FCSTD DOCUMENT  (FreeCAD 0.21R33771 (Git))
Label: key-v4_reall
License: All rights reserved
LicenseURL: https://en.wikipedia.org/wiki/All_rights_reserved
objects: Part::Part2DObjectPython×3, Sketcher::SketchObject×3, Spreadsheet::Sheet×1
note: 6 computed .brp shape members not serialized (recipe doc carries the construction recipe); baked Part::Feature solids carry a one-line shape summary decoded from their .brp

FEATURE [Spreadsheet::Sheet] Spreadsheet  label="constants"
  cells = A1(slot_height)=0.6; B1='slot height; A2(base_normal)=1.5; B2='base normal; A3(base_thin)=0.3; B3='base thin ; A4(fillet_small)=0.15; B4='fillet rounding
FEATURE [Part::Part2DObjectPython] Wire  # Draft 2D object (typed FeaturePython)
  Area = 0
  ChamferSize = 0
  Closed = false
  End = (95,2.6,0)
  FilletRadius = 0
  Length = 95.9778
  MakeFace = true
  Points = (6) [(0,0,0),(19,0,0),(38,4.8,0),(57,7,0),(76,4.8,0),(95,2.6,0)]
  Start = (0,0,0)
  Subdivisions = 0
FEATURE [Part::Part2DObjectPython] Wire001  label="main matrix wire"  # Draft 2D object (typed FeaturePython)
  Area = 0
  ChamferSize = 0
  Closed = false
  End = (95,2.6,0)
  FilletRadius = 0
  Length = 323.978
  MakeFace = false
  Points = (18) [(0,0,0),(0,-19,0),(0,-38,0),(19,-38,0),(19,-19,0),(19,0,0),(38,4.8,0),(38,-14.2,0),(38,-33.2,0),(57,-31,0),(57,-12,0),(57,7,0),(76,4.8,0),+5 more]
  Start = (0,0,0)
  Subdivisions = 0
FEATURE [Part::Part2DObjectPython] Wire002  label="horizonal matrix"  # Draft 2D object (typed FeaturePython)
  Area = 0
  ChamferSize = 0
  Closed = false
  End = (95,2.6,0)
  FilletRadius = 0
  Length = 368.271
  MakeFace = true
  Points = (20) [(0,0,0),(0,-19,0),(0,-38,0),(19,-38,0),(19,-19,0),(19,0,0),(38,4.8,0),(38,-14.2,0),(38,-33.2,0),(47,-52.4,0),(66,-52.4,0),(57,-31,0),(57,-12,0),+7 more]
  Start = (0,0,0)
  Subdivisions = 0
FEATURE [Sketcher::SketchObject] Sketch001  label="smd cutout prototype"
  FullyConstrained = true
  sketch-geometry (67):
    g0: LineSegment StartX=-9.5 StartY=-9.5 StartZ=0 EndX=9.5 EndY=-9.5 EndZ=0
    g1: LineSegment StartX=9.5 StartY=-9.5 StartZ=0 EndX=9.5 EndY=9.5 EndZ=0
    g2: LineSegment StartX=9.5 StartY=9.5 StartZ=0 EndX=-9.5 EndY=9.5 EndZ=0
    g3: LineSegment StartX=-9.5 StartY=9.5 StartZ=0 EndX=-9.5 EndY=-9.5 EndZ=0
    g4: Circle CenterX=-3.81 CenterY=2.54 CenterZ=0 NormalX=0 NormalY=0 NormalZ=1 AngleXU=0 Radius=1.5
    g5: Circle CenterX=2.54 CenterY=5.08 CenterZ=0 NormalX=0 NormalY=0 NormalZ=1 AngleXU=0 Radius=1.5
    g6: Circle CenterX=0 CenterY=0 CenterZ=0 NormalX=0 NormalY=0 NormalZ=1 AngleXU=0 Radius=2
    g7: Circle CenterX=5 CenterY=0 CenterZ=0 NormalX=0 NormalY=0 NormalZ=1 AngleXU=0 Radius=1
    g8: Circle CenterX=-5 CenterY=0 CenterZ=0 NormalX=0 NormalY=0 NormalZ=1 AngleXU=0 Radius=1
    g9: GeomPoint X=-8.5 Y=1 Z=0
    g10: GeomPoint X=-8.5 Y=4 Z=0
    g11: GeomPoint X=-6 Y=4 Z=0
    g12: GeomPoint X=-2.5 Y=1 Z=0
    g13: GeomPoint X=-0.4 Y=2.9 Z=0
    g14: GeomPoint X=4.5 Y=2.9 Z=0
    g15: GeomPoint X=4.5 Y=3.6 Z=0
    g16: GeomPoint X=7.1 Y=6.7 Z=0
    g17: GeomPoint X=-4 Y=6.7 Z=0
    g18: LineSegment StartX=-8.5 StartY=1 StartZ=0 EndX=-2.5 EndY=1 EndZ=0
    g19: LineSegment StartX=-8.5 StartY=1 StartZ=0 EndX=-8.5 EndY=4 EndZ=0
    g20: LineSegment StartX=-8.5 StartY=4 StartZ=0 EndX=-6 EndY=4 EndZ=0
    g21: LineSegment StartX=-6 StartY=4 StartZ=0 EndX=-6 EndY=4.7 EndZ=0
    g22: LineSegment StartX=-4 StartY=6.7 StartZ=0 EndX=7.1 EndY=6.7 EndZ=0
    g23: LineSegment StartX=7.1 StartY=6.7 StartZ=0 EndX=7.1 EndY=3.6 EndZ=0
    g24: LineSegment StartX=7.1 StartY=3.6 StartZ=0 EndX=4.5 EndY=3.6 EndZ=0
    g25: LineSegment StartX=4.5 StartY=2.9 StartZ=0 EndX=4.5 EndY=3.6 EndZ=0
    g26: LineSegment StartX=4.5 StartY=2.9 StartZ=0 EndX=-0.4 EndY=2.9 EndZ=0
    g27: ArcOfCircle CenterX=-0.4 CenterY=0.789474 CenterZ=0 NormalX=0 NormalY=0 NormalZ=1 AngleXU=0 Radius=2.11053 StartAngle=1.5708 EndAngle=3.04168
    g28: LineSegment StartX=6.85 StartY=2.35 StartZ=0 EndX=6.85 EndY=-2.35 EndZ=0
    g29: LineSegment StartX=6.85 StartY=-2.35 StartZ=0 EndX=9.15 EndY=-2.35 EndZ=0
    g30: LineSegment StartX=9.15 StartY=-2.35 StartZ=0 EndX=9.15 EndY=2.35 EndZ=0
    g31: ArcOfCircle CenterX=-4 CenterY=4.7 CenterZ=0 NormalX=0 NormalY=0 NormalZ=1 AngleXU=0 Radius=2 StartAngle=1.5708 EndAngle=3.14159
    g32: LineSegment StartX=6.85 StartY=2.35 StartZ=0 EndX=9.15 EndY=2.35 EndZ=0
    g33: LineSegment StartX=-8.8 StartY=0.8 StartZ=0 EndX=-8.8 EndY=4.2 EndZ=0
    g34: LineSegment StartX=-8.3 StartY=4.7 StartZ=0 EndX=-7.1607 EndY=4.7 EndZ=0
    g35: LineSegment StartX=-4 StartY=7.4 StartZ=0 EndX=7.3 EndY=7.4 EndZ=0
    g36: LineSegment StartX=7.8 StartY=6.9 StartZ=0 EndX=7.8 EndY=3.55 EndZ=0
    g37: LineSegment StartX=9.5 StartY=2.55 StartZ=0 EndX=9.5 EndY=-2.55 EndZ=0
    g38: LineSegment StartX=9 StartY=-3.05 StartZ=0 EndX=6.65 EndY=-3.05 EndZ=0
    g39: LineSegment StartX=-8.3 StartY=0.3 StartZ=0 EndX=-7.19089 EndY=0.3 EndZ=0
    g40: ArcOfCircle CenterX=-5 CenterY=0 CenterZ=0 NormalX=0 NormalY=0 NormalZ=1 AngleXU=0 Radius=1.7 StartAngle=3.23263 EndAngle=4.71239
    g41: ArcOfCircle CenterX=0 CenterY=0 CenterZ=0 NormalX=0 NormalY=0 NormalZ=1 AngleXU=0 Radius=2.7 StartAngle=3.89963 EndAngle=5.52514
    g42: LineSegment StartX=-5 StartY=-1.7 StartZ=0 EndX=-2.32379 EndY=-1.7 EndZ=0
    g43: LineSegment StartX=6.15 StartY=-2.55 StartZ=0 EndX=6.15 EndY=-2.2 EndZ=0
    g44: LineSegment StartX=2.32379 StartY=-1.7 StartZ=0 EndX=5.65 EndY=-1.7 EndZ=0
    g45: ArcOfCircle CenterX=-4 CenterY=4.7 CenterZ=0 NormalX=0 NormalY=0 NormalZ=1 AngleXU=0 Radius=2.7 StartAngle=1.5708 EndAngle=2.9847
    g46: ArcOfCircle CenterX=-2.32379 CenterY=-2.2 CenterZ=0 NormalX=0 NormalY=0 NormalZ=1 AngleXU=0 Radius=0.5 StartAngle=0.758041 EndAngle=1.5708
    g47: ArcOfCircle CenterX=2.32379 CenterY=-2.2 CenterZ=0 NormalX=0 NormalY=0 NormalZ=1 AngleXU=0 Radius=0.5 StartAngle=1.5708 EndAngle=2.38355
    g48: ArcOfCircle CenterX=5.65 CenterY=-2.2 CenterZ=0 NormalX=0 NormalY=0 NormalZ=1 AngleXU=0 Radius=0.5 StartAngle=0 EndAngle=1.5708
    g49: GeomPoint X=6.15 Y=-1.7 Z=0
    g50: ArcOfCircle CenterX=6.65 CenterY=-2.55 CenterZ=0 NormalX=0 NormalY=0 NormalZ=1 AngleXU=0 Radius=0.5 StartAngle=3.14159 EndAngle=4.71239
    g51: GeomPoint X=6.15 Y=-3.05 Z=0
    g52: ArcOfCircle CenterX=9 CenterY=-2.55 CenterZ=0 NormalX=0 NormalY=0 NormalZ=1 AngleXU=0 Radius=0.5 StartAngle=4.71239 EndAngle=6.28319
    g53: GeomPoint X=9.5 Y=-3.05 Z=0
    g54: LineSegment StartX=8.3 StartY=3.05 StartZ=0 EndX=9 EndY=3.05 EndZ=0
    g55: ArcOfCircle CenterX=9 CenterY=2.55 CenterZ=0 NormalX=0 NormalY=0 NormalZ=1 AngleXU=0 Radius=0.5 StartAngle=3e-16 EndAngle=1.5708
    g56: GeomPoint X=9.5 Y=3.05 Z=0
    g57: ArcOfCircle CenterX=8.3 CenterY=3.55 CenterZ=0 NormalX=0 NormalY=0 NormalZ=1 AngleXU=0 Radius=0.5 StartAngle=3.14159 EndAngle=4.71239
    g58: GeomPoint X=7.8 Y=3.05 Z=0
    g59: ArcOfCircle CenterX=7.3 CenterY=6.9 CenterZ=0 NormalX=0 NormalY=0 NormalZ=1 AngleXU=0 Radius=0.5 StartAngle=-9e-16 EndAngle=1.5708
    g60: GeomPoint X=7.8 Y=7.4 Z=0
    g61: ArcOfCircle CenterX=-7.1607 CenterY=5.2 CenterZ=0 NormalX=0 NormalY=0 NormalZ=1 AngleXU=0 Radius=0.5 StartAngle=4.71239 EndAngle=6.12629
    g62: ArcOfCircle CenterX=-8.3 CenterY=4.2 CenterZ=0 NormalX=0 NormalY=0 NormalZ=1 AngleXU=0 Radius=0.5 StartAngle=1.5708 EndAngle=3.14159
    g63: GeomPoint X=-8.8 Y=4.7 Z=0
    g64: ArcOfCircle CenterX=-8.3 CenterY=0.8 CenterZ=0 NormalX=0 NormalY=0 NormalZ=1 AngleXU=0 Radius=0.5 StartAngle=3.14159 EndAngle=4.71239
    g65: GeomPoint X=-8.8 Y=0.3 Z=0
    g66: ArcOfCircle CenterX=-7.19089 CenterY=-0.2 CenterZ=0 NormalX=0 NormalY=0 NormalZ=1 AngleXU=0 Radius=0.5 StartAngle=0.0910348 EndAngle=1.5708
  constraints (157):
    c: Coincident(g2,g3)
    c: Horizontal(g0)
    c: Horizontal(g2)
    c: Vertical(g1)
    c: PointOnObject(g7,g-1)
    c: Equal(g4,g5)
    c: Symmetric(g7,g8,g-2)
    c: Equal(g8,g7)
    c: DistanceX(g-1,g5) = 2.54
    c: Distance(g5,g-1) = 5.08
    c: DistanceX(g2,g2) = 19
    c: Equal(g2,g3)
    c: Distance(g4,g-2) = 3.81
    c: Distance(g4,g-1) = 2.54
    c: Distance(g8,g-2) = 5
    c: Distance(g9,g-1) = 1
    c: Coincident(g18,g9)
    c: Coincident(g18,g12)
    c: Horizontal(g18)
    c: Distance(g9,g-2) = 8.5
    c: Coincident(g19,g9)
    c: Coincident(g19,g10)
    c: Vertical(g19)
    c: Distance(g10,g-1) = 4
    c: Coincident(g20,g10)
    c: Coincident(g20,g11)
    c: Horizontal(g20)
    c: Distance(g11,g-2) = 6
    c: Distance(g17,g-2) = 4
    c: DistanceY(g-1,g17) = 6.7
    c: Coincident(g21,g11)
    c: Vertical(g21)
    c: Coincident(g22,g17)
    c: Coincident(g22,g16)
    c: Horizontal(g22)
    c: DistanceX(g-1,g16) = 7.1
    c: Coincident(g23,g16)
    c: Vertical(g23)
    c: Distance(g23,g-1) = 3.6
    c: Coincident(g24,g23)
    c: Coincident(g24,g15)
    c: Coincident(g25,g14)
    c: Coincident(g25,g15)
    c: Coincident(g26,g14)
    c: Coincident(g26,g13)
    c: Horizontal(g24)
    c: Horizontal(g26)
    c: Vertical(g25)
    c: Distance(g-2,g25) = 4.5
    c: Distance(g14,g-1) = 2.9
    c: Distance(g13,g-2) = 0.4
    c: Distance(g12,g-2) = 2.5
    c: Coincident(g27,g13)
    c: Coincident(g27,g12)
    c: Diameter(g5) = 3
    c: Diameter(g8) = 2
    c: Diameter(g6) = 4
    c: Vertical(g30)
    c: Horizontal(g29)
    c: Distance(g28,g-2) = 6.85
    c: Distance(g28,g-1) = 2.35
    c: Symmetric(g28,g28,g-1)
    c: Vertical(g3)
    c: Coincident(g31,g17)
    c: Tangent(g31,g21) = 1.5708
    c: Coincident(g32,g28)
    c: Coincident(g32,g30)
    c: Horizontal(g32)
    c: Coincident(g6,g-1)
    c: Symmetric(g0,g1,g6)
    c: Coincident(g3,g0)
    c: Coincident(g2,g1)
    c: Coincident(g1,g0)
    c: DistanceX(g29,g29) = 2.3
    c: Coincident(g29,g30)
    c: Coincident(g29,g28)
    c: Tangent(g27,g26)
    c: Tangent(g31,g22)
    c: Vertical(g33)
    c: Horizontal(g34)
    c: Horizontal(g35)
    c: Vertical(g36)
    c: PointOnObject(g56,g1)
    c: PointOnObject(g53,g1)
    c: Horizontal(g38)
    c: Horizontal(g39)
    c: Distance(g20,g34) = 0.7
    c: Distance(g65,g19) = 0.3
    c: Distance(g18,g39) = 0.7
    c: Coincident(g40,g8)
    c: Coincident(g41,g6)
    c: Horizontal(g42)
    c: Vertical(g43)
    c: Tangent(g44,g42)
    c: Distance(g28,g43) = 0.7
    c: Distance(g53,g29) = 0.7
    c: Tangent(g42,g40) = -1.5708
    c: Distance(g23,g36) = 0.7
    c: Distance(g35,g22) = 0.7
    c: Coincident(g45,g31)
    c: Tangent(g45,g35) = 1.5708
    c: Tangent(g42,g46) = 1.5708
    c: Tangent(g41,g46) = 1.5708
    c: Tangent(g41,g47) = 1.5708
    c: Tangent(g44,g47) = 1.5708
    c: PointOnObject(g49,g44)
    c: PointOnObject(g49,g43)
    c: Tangent(g44,g48) = 1.5708
    c: Tangent(g43,g48) = -1.5708
    c: PointOnObject(g51,g43)
    c: PointOnObject(g51,g38)
    c: Tangent(g43,g50) = 1.5708
    c: Tangent(g38,g50) = 1.5708
    c: PointOnObject(g53,g38)
    c: PointOnObject(g53,g37)
    c: Tangent(g38,g52) = 1.5708
    c: Tangent(g37,g52) = 1.5708
    c: Horizontal(g54)
    c: Distance(g32,g54) = 0.7
    c: PointOnObject(g56,g37)
    c: PointOnObject(g56,g54)
    c: Tangent(g37,g55) = 1.5708
    c: Tangent(g54,g55) = 1.5708
    c: PointOnObject(g58,g54)
    c: PointOnObject(g58,g36)
    c: Tangent(g54,g57) = -1.5708
    c: Tangent(g36,g57) = -1.5708
    c: PointOnObject(g60,g35)
    c: PointOnObject(g60,g36)
    c: Tangent(g35,g59) = 1.5708
    c: Tangent(g36,g59) = 1.5708
    c: Tangent(g34,g61) = -1.5708
    c: Tangent(g45,g61) = 1.5708
    c: PointOnObject(g63,g34)
    c: PointOnObject(g63,g33)
    c: Tangent(g34,g62) = 1.5708
    c: Tangent(g33,g62) = 1.5708
    c: PointOnObject(g65,g39)
    c: PointOnObject(g65,g33)
    c: Tangent(g39,g64) = -1.5708
    c: Tangent(g33,g64) = 1.5708
    c: Tangent(g40,g66) = 1.5708
    c: Tangent(g39,g66) = 1.5708
    c: Radius(g46) = 0.5
    c: Equal(g66,g64)
    c: Equal(g64,g46)
    c: Equal(g46,g47)
    c: Equal(g47,g48)
    c: Equal(g48,g50)
    c: Equal(g50,g57)
    c: Equal(g57,g59)
    c: Equal(g59,g61)
    c: Equal(g61,g62)
    c: Equal(g57,g55)
    c: Equal(g52,g50)
    c: Distance(g40,g8) = 0.7
    c: Distance(g41,g6) = 0.7
FEATURE [Sketcher::SketchObject] Sketch003  label="smd cutout"
  FullyConstrained = false
  sketch-geometry (61):
    g0: GeomPoint X=-8.5 Y=1 Z=0
    g1: GeomPoint X=-8.5 Y=4 Z=0
    g2: GeomPoint X=-6 Y=4 Z=0
    g3: GeomPoint X=-2.5 Y=1 Z=0
    g4: GeomPoint X=-0.4 Y=2.9 Z=0
    g5: GeomPoint X=4.5 Y=2.9 Z=0
    g6: GeomPoint X=4.5 Y=3.6 Z=0
    g7: GeomPoint X=7.1 Y=6.7 Z=0
    g8: GeomPoint X=-4 Y=6.7 Z=0
    g9: LineSegment StartX=-8.8 StartY=0.8 StartZ=0 EndX=-8.8 EndY=4.2 EndZ=0
    g10: LineSegment StartX=-8.3 StartY=4.7 StartZ=0 EndX=-7.1607 EndY=4.7 EndZ=0
    g11: LineSegment StartX=-4 StartY=7.4 StartZ=0 EndX=7.3 EndY=7.4 EndZ=0
    g12: LineSegment StartX=7.8 StartY=6.9 StartZ=0 EndX=7.8 EndY=3.55 EndZ=0
    g13: LineSegment StartX=9.5 StartY=2.55 StartZ=0 EndX=9.5 EndY=-2.55 EndZ=0
    g14: LineSegment StartX=9 StartY=-3.05 StartZ=0 EndX=6.65 EndY=-3.05 EndZ=0
    g15: LineSegment StartX=-8.3 StartY=0.3 StartZ=0 EndX=-7.19089 EndY=0.3 EndZ=0
    g16: ArcOfCircle CenterX=-5 CenterY=0 CenterZ=0 NormalX=0 NormalY=0 NormalZ=1 AngleXU=0 Radius=1.7 StartAngle=3.23263 EndAngle=4.71239
    g17: ArcOfCircle CenterX=0 CenterY=0 CenterZ=0 NormalX=0 NormalY=0 NormalZ=1 AngleXU=0 Radius=2.7 StartAngle=3.89963 EndAngle=5.52514
    g18: LineSegment StartX=-5 StartY=-1.7 StartZ=0 EndX=-2.32379 EndY=-1.7 EndZ=0
    g19: LineSegment StartX=6.15 StartY=-2.55 StartZ=0 EndX=6.15 EndY=-2.2 EndZ=0
    g20: LineSegment StartX=2.32379 StartY=-1.7 StartZ=0 EndX=5.65 EndY=-1.7 EndZ=0
    g21: ArcOfCircle CenterX=-4 CenterY=4.7 CenterZ=0 NormalX=0 NormalY=0 NormalZ=1 AngleXU=0 Radius=2.7 StartAngle=1.5708 EndAngle=2.9847
    g22: ArcOfCircle CenterX=-2.32379 CenterY=-2.2 CenterZ=0 NormalX=0 NormalY=0 NormalZ=1 AngleXU=0 Radius=0.5 StartAngle=0.758041 EndAngle=1.5708
    g23: ArcOfCircle CenterX=2.32379 CenterY=-2.2 CenterZ=0 NormalX=0 NormalY=0 NormalZ=1 AngleXU=0 Radius=0.5 StartAngle=1.5708 EndAngle=2.38355
    g24: ArcOfCircle CenterX=5.65 CenterY=-2.2 CenterZ=0 NormalX=0 NormalY=0 NormalZ=1 AngleXU=0 Radius=0.5 StartAngle=0 EndAngle=1.5708
    g25: GeomPoint X=6.15 Y=-1.7 Z=0
    g26: ArcOfCircle CenterX=6.65 CenterY=-2.55 CenterZ=0 NormalX=0 NormalY=0 NormalZ=1 AngleXU=0 Radius=0.5 StartAngle=3.14159 EndAngle=4.71239
    g27: GeomPoint X=6.15 Y=-3.05 Z=0
    g28: ArcOfCircle CenterX=9 CenterY=-2.55 CenterZ=0 NormalX=0 NormalY=0 NormalZ=1 AngleXU=0 Radius=0.5 StartAngle=4.71239 EndAngle=6.28319
    g29: GeomPoint X=9.5 Y=-3.05 Z=0
    g30: LineSegment StartX=8.3 StartY=3.05 StartZ=0 EndX=9 EndY=3.05 EndZ=0
    g31: ArcOfCircle CenterX=9 CenterY=2.55 CenterZ=0 NormalX=0 NormalY=0 NormalZ=1 AngleXU=0 Radius=0.5 StartAngle=3e-16 EndAngle=1.5708
    g32: GeomPoint X=9.5 Y=3.05 Z=0
    g33: ArcOfCircle CenterX=8.3 CenterY=3.55 CenterZ=0 NormalX=0 NormalY=0 NormalZ=1 AngleXU=0 Radius=0.5 StartAngle=3.14159 EndAngle=4.71239
    g34: GeomPoint X=7.8 Y=3.05 Z=0
    g35: ArcOfCircle CenterX=7.3 CenterY=6.9 CenterZ=0 NormalX=0 NormalY=0 NormalZ=1 AngleXU=0 Radius=0.5 StartAngle=-9e-16 EndAngle=1.5708
    g36: GeomPoint X=7.8 Y=7.4 Z=0
    g37: ArcOfCircle CenterX=-7.1607 CenterY=5.2 CenterZ=0 NormalX=0 NormalY=0 NormalZ=1 AngleXU=0 Radius=0.5 StartAngle=4.71239 EndAngle=6.12629
    g38: ArcOfCircle CenterX=-8.3 CenterY=4.2 CenterZ=0 NormalX=0 NormalY=0 NormalZ=1 AngleXU=0 Radius=0.5 StartAngle=1.5708 EndAngle=3.14159
    g39: GeomPoint X=-8.8 Y=4.7 Z=0
    g40: ArcOfCircle CenterX=-8.3 CenterY=0.8 CenterZ=0 NormalX=0 NormalY=0 NormalZ=1 AngleXU=0 Radius=0.5 StartAngle=3.14159 EndAngle=4.71239
    g41: GeomPoint X=-8.8 Y=0.3 Z=0
    g42: ArcOfCircle CenterX=-7.19089 CenterY=-0.2 CenterZ=0 NormalX=0 NormalY=0 NormalZ=1 AngleXU=0 Radius=0.5 StartAngle=0.0910348 EndAngle=1.5708
    g43: ArcOfCircle CenterX=-5 CenterY=0 CenterZ=0 NormalX=0 NormalY=0 NormalZ=1 AngleXU=0 Radius=3.2 StartAngle=3.52599 EndAngle=4.71239
    g44: LineSegment StartX=-5 StartY=-3.2 StartZ=0 EndX=-2.72029 EndY=-3.2 EndZ=0
    g45: ArcOfCircle CenterX=0 CenterY=0 CenterZ=0 NormalX=0 NormalY=0 NormalZ=1 AngleXU=0 Radius=4.2 StartAngle=4.00784 EndAngle=5.41694
    g46: LineSegment StartX=2.72029 StartY=-3.2 StartZ=0 EndX=4.75857 EndY=-3.2 EndZ=0
    g47: ArcOfCircle CenterX=6.65 CenterY=-2.55 CenterZ=0 NormalX=0 NormalY=0 NormalZ=1 AngleXU=0 Radius=2 StartAngle=3.4726 EndAngle=4.71239
    g48: LineSegment StartX=9 StartY=-4.55 StartZ=0 EndX=6.65 EndY=-4.55 EndZ=0
    g49: ArcOfCircle CenterX=9 CenterY=-2.55 CenterZ=0 NormalX=0 NormalY=0 NormalZ=1 AngleXU=0 Radius=2 StartAngle=4.71239 EndAngle=6.28319
    g50: LineSegment StartX=11 StartY=2.55 StartZ=0 EndX=11 EndY=-2.55 EndZ=0
    g51: ArcOfCircle CenterX=9 CenterY=2.55 CenterZ=0 NormalX=0 NormalY=0 NormalZ=1 AngleXU=0 Radius=2 StartAngle=0 EndAngle=1.42023
    g52: LineSegment StartX=9.3 StartY=6.9 StartZ=0 EndX=9.3 EndY=4.52737 EndZ=0
    g53: ArcOfCircle CenterX=7.3 CenterY=6.9 CenterZ=0 NormalX=0 NormalY=0 NormalZ=1 AngleXU=0 Radius=2 StartAngle=4e-16 EndAngle=1.5708
    g54: LineSegment StartX=-4 StartY=8.9 StartZ=0 EndX=7.3 EndY=8.9 EndZ=0
    g55: ArcOfCircle CenterX=-4 CenterY=4.7 CenterZ=0 NormalX=0 NormalY=0 NormalZ=1 AngleXU=0 Radius=4.2 StartAngle=1.5708 EndAngle=2.77639
    g56: LineSegment StartX=-8.3 StartY=6.2 StartZ=0 EndX=-7.92301 EndY=6.2 EndZ=0
    g57: ArcOfCircle CenterX=-8.3 CenterY=4.2 CenterZ=0 NormalX=0 NormalY=0 NormalZ=1 AngleXU=0 Radius=2 StartAngle=1.5708 EndAngle=3.14159
    g58: LineSegment StartX=-10.3 StartY=0.8 StartZ=0 EndX=-10.3 EndY=4.2 EndZ=0
    g59: ArcOfCircle CenterX=-8.3 CenterY=0.8 CenterZ=0 NormalX=0 NormalY=0 NormalZ=1 AngleXU=0 Radius=2 StartAngle=3.14159 EndAngle=4.71239
    g60: LineSegment StartX=-8.3 StartY=-1.2 StartZ=0 EndX=-7.96648 EndY=-1.2 EndZ=0
  constraints (137):
    c: Distance(g0,g-1) = 1
    c: Distance(g0,g-2) = 8.5
    c: Distance(g1,g-1) = 4
    c: Distance(g2,g-2) = 6
    c: Distance(g8,g-2) = 4
    c: DistanceY(g-1,g8) = 6.7
    c: DistanceX(g-1,g7) = 7.1
    c: Distance(g5,g-1) = 2.9
    c: Distance(g4,g-2) = 0.4
    c: Distance(g3,g-2) = 2.5
    c: Vertical(g9)
    c: Horizontal(g10)
    c: Horizontal(g11)
    c: Vertical(g12)
    c: Horizontal(g14)
    c: Horizontal(g15)
    c: Distance(g1,g10) = 0.7
    c: Distance(g0,g15) = 0.7
    c: Horizontal(g18)
    c: Vertical(g19)
    c: Tangent(g20,g18)
    c: Tangent(g18,g16) = -1.5708
    c: Distance(g7,g12) = 0.7
    c: Tangent(g21,g11) = 1.5708
    c: Tangent(g18,g22) = 1.5708
    c: Tangent(g17,g22) = 1.5708
    c: Tangent(g17,g23) = 1.5708
    c: Tangent(g20,g23) = 1.5708
    c: PointOnObject(g25,g20)
    c: PointOnObject(g25,g19)
    c: Tangent(g20,g24) = 1.5708
    c: Tangent(g19,g24) = -1.5708
    c: PointOnObject(g27,g19)
    c: PointOnObject(g27,g14)
    c: Tangent(g19,g26) = 1.5708
    c: Tangent(g14,g26) = 1.5708
    c: PointOnObject(g29,g14)
    c: PointOnObject(g29,g13)
    c: Tangent(g14,g28) = 1.5708
    c: Tangent(g13,g28) = 1.5708
    c: Horizontal(g30)
    c: PointOnObject(g32,g13)
    c: PointOnObject(g32,g30)
    c: Tangent(g13,g31) = 1.5708
    c: Tangent(g30,g31) = 1.5708
    c: PointOnObject(g34,g30)
    c: PointOnObject(g34,g12)
    c: Tangent(g30,g33) = -1.5708
    c: Tangent(g12,g33) = -1.5708
    c: PointOnObject(g36,g11)
    c: PointOnObject(g36,g12)
    c: Tangent(g11,g35) = 1.5708
    c: Tangent(g12,g35) = 1.5708
    c: Tangent(g10,g37) = -1.5708
    c: Tangent(g21,g37) = 1.5708
    c: PointOnObject(g39,g10)
    c: PointOnObject(g39,g9)
    c: Tangent(g10,g38) = 1.5708
    c: Tangent(g9,g38) = 1.5708
    c: PointOnObject(g41,g15)
    c: PointOnObject(g41,g9)
    c: Tangent(g15,g40) = -1.5708
    c: Tangent(g9,g40) = 1.5708
    c: Tangent(g16,g42) = 1.5708
    c: Tangent(g15,g42) = 1.5708
    c: Radius(g22) = 0.5
    c: Equal(g42,g40)
    c: Equal(g40,g22)
    c: Equal(g22,g23)
    c: Equal(g23,g24)
    c: Equal(g24,g26)
    c: Equal(g26,g33)
    c: Equal(g33,g35)
    c: Equal(g35,g37)
    c: Equal(g37,g38)
    c: Equal(g33,g31)
    c: Equal(g28,g26)
    c: Tangent(g43,g44) = -1.5708
    c: Coincident(g43,g60)
    c: Coincident(g44,g45)
    c: Coincident(g45,g46)
    c: Coincident(g46,g47)
    c: Tangent(g47,g48) = 1.5708
    c: Tangent(g48,g49) = 1.5708
    c: Tangent(g49,g50) = 1.5708
    c: Tangent(g50,g51) = 1.5708
    c: Coincident(g51,g52)
    c: Tangent(g52,g53) = 1.5708
    c: Tangent(g53,g54) = 1.5708
    c: Tangent(g54,g55) = 1.5708
    c: Coincident(g55,g56)
    c: Tangent(g56,g57) = 1.5708
    c: Tangent(g57,g58) = 1.5708
    c: Tangent(g58,g59) = 1.5708
    c: Tangent(g59,g60) = -1.5708
    c: Block(g55)
    c: Block(g54)
    c: Block(g53)
    c: Block(g52)
    c: Block(g51)
    c: Block(g50)
    c: Block(g49)
    c: Block(g48)
    c: Block(g47)
    c: Block(g46)
    c: Block(g45)
    c: Block(g44)
    c: Block(g43)
    c: Block(g60)
    c: Block(g59)
    c: Block(g58)
    c: Block(g57)
    c: Block(g21)
    c: Block(g37)
    c: Block(g10)
    c: Block(g38)
    c: Block(g9)
    c: Block(g40)
    c: Block(g15)
    c: Block(g42)
    c: Block(g16)
    c: Block(g18)
    c: Block(g22)
    c: Block(g17)
    c: Block(g23)
    c: Block(g20)
    c: Block(g24)
    c: Block(g26)
    c: Block(g19)
    c: Block(g14)
    c: Block(g28)
    c: Block(g13)
    c: Block(g31)
    c: Block(g30)
    c: Block(g33)
    c: Block(g12)
    c: Block(g35)
FEATURE [Sketcher::SketchObject] Sketch004  label="smd cutout offset"
  FullyConstrained = false
  sketch-geometry (61):
    g0: GeomPoint X=-8.5 Y=1 Z=0
    g1: GeomPoint X=-8.5 Y=4 Z=0
    g2: GeomPoint X=-6 Y=4 Z=0
    g3: GeomPoint X=-2.5 Y=1 Z=0
    g4: GeomPoint X=-0.4 Y=2.9 Z=0
    g5: GeomPoint X=4.5 Y=2.9 Z=0
    g6: GeomPoint X=4.5 Y=3.6 Z=0
    g7: GeomPoint X=7.1 Y=6.7 Z=0
    g8: GeomPoint X=-4 Y=6.7 Z=0
    g9: LineSegment StartX=-8.8 StartY=0.8 StartZ=0 EndX=-8.8 EndY=4.2 EndZ=0
    g10: LineSegment StartX=-8.3 StartY=4.7 StartZ=0 EndX=-7.1607 EndY=4.7 EndZ=0
    g11: LineSegment StartX=-4 StartY=7.4 StartZ=0 EndX=7.3 EndY=7.4 EndZ=0
    g12: LineSegment StartX=7.8 StartY=6.9 StartZ=0 EndX=7.8 EndY=3.55 EndZ=0
    g13: LineSegment StartX=9.5 StartY=2.55 StartZ=0 EndX=9.5 EndY=-2.55 EndZ=0
    g14: LineSegment StartX=9 StartY=-3.05 StartZ=0 EndX=6.65 EndY=-3.05 EndZ=0
    g15: LineSegment StartX=-8.3 StartY=0.3 StartZ=0 EndX=-7.19089 EndY=0.3 EndZ=0
    g16: ArcOfCircle CenterX=-5 CenterY=0 CenterZ=0 NormalX=0 NormalY=0 NormalZ=1 AngleXU=0 Radius=1.7 StartAngle=3.23263 EndAngle=4.71239
    g17: ArcOfCircle CenterX=0 CenterY=0 CenterZ=0 NormalX=0 NormalY=0 NormalZ=1 AngleXU=0 Radius=2.7 StartAngle=3.89963 EndAngle=5.52514
    g18: LineSegment StartX=-5 StartY=-1.7 StartZ=0 EndX=-2.32379 EndY=-1.7 EndZ=0
    g19: LineSegment StartX=6.15 StartY=-2.55 StartZ=0 EndX=6.15 EndY=-2.2 EndZ=0
    g20: LineSegment StartX=2.32379 StartY=-1.7 StartZ=0 EndX=5.65 EndY=-1.7 EndZ=0
    g21: ArcOfCircle CenterX=-4 CenterY=4.7 CenterZ=0 NormalX=0 NormalY=0 NormalZ=1 AngleXU=0 Radius=2.7 StartAngle=1.5708 EndAngle=2.9847
    g22: ArcOfCircle CenterX=-2.32379 CenterY=-2.2 CenterZ=0 NormalX=0 NormalY=0 NormalZ=1 AngleXU=0 Radius=0.5 StartAngle=0.758041 EndAngle=1.5708
    g23: ArcOfCircle CenterX=2.32379 CenterY=-2.2 CenterZ=0 NormalX=0 NormalY=0 NormalZ=1 AngleXU=0 Radius=0.5 StartAngle=1.5708 EndAngle=2.38355
    g24: ArcOfCircle CenterX=5.65 CenterY=-2.2 CenterZ=0 NormalX=0 NormalY=0 NormalZ=1 AngleXU=0 Radius=0.5 StartAngle=0 EndAngle=1.5708
    g25: GeomPoint X=6.15 Y=-1.7 Z=0
    g26: ArcOfCircle CenterX=6.65 CenterY=-2.55 CenterZ=0 NormalX=0 NormalY=0 NormalZ=1 AngleXU=0 Radius=0.5 StartAngle=3.14159 EndAngle=4.71239
    g27: GeomPoint X=6.15 Y=-3.05 Z=0
    g28: ArcOfCircle CenterX=9 CenterY=-2.55 CenterZ=0 NormalX=0 NormalY=0 NormalZ=1 AngleXU=0 Radius=0.5 StartAngle=4.71239 EndAngle=6.28319
    g29: GeomPoint X=9.5 Y=-3.05 Z=0
    g30: LineSegment StartX=8.3 StartY=3.05 StartZ=0 EndX=9 EndY=3.05 EndZ=0
    g31: ArcOfCircle CenterX=9 CenterY=2.55 CenterZ=0 NormalX=0 NormalY=0 NormalZ=1 AngleXU=0 Radius=0.5 StartAngle=3e-16 EndAngle=1.5708
    g32: GeomPoint X=9.5 Y=3.05 Z=0
    g33: ArcOfCircle CenterX=8.3 CenterY=3.55 CenterZ=0 NormalX=0 NormalY=0 NormalZ=1 AngleXU=0 Radius=0.5 StartAngle=3.14159 EndAngle=4.71239
    g34: GeomPoint X=7.8 Y=3.05 Z=0
    g35: ArcOfCircle CenterX=7.3 CenterY=6.9 CenterZ=0 NormalX=0 NormalY=0 NormalZ=1 AngleXU=0 Radius=0.5 StartAngle=-9e-16 EndAngle=1.5708
    g36: GeomPoint X=7.8 Y=7.4 Z=0
    g37: ArcOfCircle CenterX=-7.1607 CenterY=5.2 CenterZ=0 NormalX=0 NormalY=0 NormalZ=1 AngleXU=0 Radius=0.5 StartAngle=4.71239 EndAngle=6.12629
    g38: ArcOfCircle CenterX=-8.3 CenterY=4.2 CenterZ=0 NormalX=0 NormalY=0 NormalZ=1 AngleXU=0 Radius=0.5 StartAngle=1.5708 EndAngle=3.14159
    g39: GeomPoint X=-8.8 Y=4.7 Z=0
    g40: ArcOfCircle CenterX=-8.3 CenterY=0.8 CenterZ=0 NormalX=0 NormalY=0 NormalZ=1 AngleXU=0 Radius=0.5 StartAngle=3.14159 EndAngle=4.71239
    g41: GeomPoint X=-8.8 Y=0.3 Z=0
    g42: ArcOfCircle CenterX=-7.19089 CenterY=-0.2 CenterZ=0 NormalX=0 NormalY=0 NormalZ=1 AngleXU=0 Radius=0.5 StartAngle=0.0910348 EndAngle=1.5708
    g43: ArcOfCircle CenterX=-5 CenterY=0 CenterZ=0 NormalX=0 NormalY=0 NormalZ=1 AngleXU=0 Radius=3.2 StartAngle=3.52599 EndAngle=4.71239
    g44: LineSegment StartX=-5 StartY=-3.2 StartZ=0 EndX=-2.72029 EndY=-3.2 EndZ=0
    g45: ArcOfCircle CenterX=0 CenterY=0 CenterZ=0 NormalX=0 NormalY=0 NormalZ=1 AngleXU=0 Radius=4.2 StartAngle=4.00784 EndAngle=5.41694
    g46: LineSegment StartX=2.72029 StartY=-3.2 StartZ=0 EndX=4.75857 EndY=-3.2 EndZ=0
    g47: ArcOfCircle CenterX=6.65 CenterY=-2.55 CenterZ=0 NormalX=0 NormalY=0 NormalZ=1 AngleXU=0 Radius=2 StartAngle=3.4726 EndAngle=4.71239
    g48: LineSegment StartX=9 StartY=-4.55 StartZ=0 EndX=6.65 EndY=-4.55 EndZ=0
    g49: ArcOfCircle CenterX=9 CenterY=-2.55 CenterZ=0 NormalX=0 NormalY=0 NormalZ=1 AngleXU=0 Radius=2 StartAngle=4.71239 EndAngle=6.28319
    g50: LineSegment StartX=11 StartY=2.55 StartZ=0 EndX=11 EndY=-2.55 EndZ=0
    g51: ArcOfCircle CenterX=9 CenterY=2.55 CenterZ=0 NormalX=0 NormalY=0 NormalZ=1 AngleXU=0 Radius=2 StartAngle=0 EndAngle=1.42023
    g52: LineSegment StartX=9.3 StartY=6.9 StartZ=0 EndX=9.3 EndY=4.52737 EndZ=0
    g53: ArcOfCircle CenterX=7.3 CenterY=6.9 CenterZ=0 NormalX=0 NormalY=0 NormalZ=1 AngleXU=0 Radius=2 StartAngle=4e-16 EndAngle=1.5708
    g54: LineSegment StartX=-4 StartY=8.9 StartZ=0 EndX=7.3 EndY=8.9 EndZ=0
    g55: ArcOfCircle CenterX=-4 CenterY=4.7 CenterZ=0 NormalX=0 NormalY=0 NormalZ=1 AngleXU=0 Radius=4.2 StartAngle=1.5708 EndAngle=2.77639
    g56: LineSegment StartX=-8.3 StartY=6.2 StartZ=0 EndX=-7.92301 EndY=6.2 EndZ=0
    g57: ArcOfCircle CenterX=-8.3 CenterY=4.2 CenterZ=0 NormalX=0 NormalY=0 NormalZ=1 AngleXU=0 Radius=2 StartAngle=1.5708 EndAngle=3.14159
    g58: LineSegment StartX=-10.3 StartY=0.8 StartZ=0 EndX=-10.3 EndY=4.2 EndZ=0
    g59: ArcOfCircle CenterX=-8.3 CenterY=0.8 CenterZ=0 NormalX=0 NormalY=0 NormalZ=1 AngleXU=0 Radius=2 StartAngle=3.14159 EndAngle=4.71239
    g60: LineSegment StartX=-8.3 StartY=-1.2 StartZ=0 EndX=-7.96648 EndY=-1.2 EndZ=0
  constraints (137):
    c: Distance(g0,g-1) = 1
    c: Distance(g0,g-2) = 8.5
    c: Distance(g1,g-1) = 4
    c: Distance(g2,g-2) = 6
    c: Distance(g8,g-2) = 4
    c: DistanceY(g-1,g8) = 6.7
    c: DistanceX(g-1,g7) = 7.1
    c: Distance(g5,g-1) = 2.9
    c: Distance(g4,g-2) = 0.4
    c: Distance(g3,g-2) = 2.5
    c: Vertical(g9)
    c: Horizontal(g10)
    c: Horizontal(g11)
    c: Vertical(g12)
    c: Horizontal(g14)
    c: Horizontal(g15)
    c: Distance(g1,g10) = 0.7
    c: Distance(g0,g15) = 0.7
    c: Horizontal(g18)
    c: Vertical(g19)
    c: Tangent(g20,g18)
    c: Tangent(g18,g16) = -1.5708
    c: Distance(g7,g12) = 0.7
    c: Tangent(g21,g11) = 1.5708
    c: Tangent(g18,g22) = 1.5708
    c: Tangent(g17,g22) = 1.5708
    c: Tangent(g17,g23) = 1.5708
    c: Tangent(g20,g23) = 1.5708
    c: PointOnObject(g25,g20)
    c: PointOnObject(g25,g19)
    c: Tangent(g20,g24) = 1.5708
    c: Tangent(g19,g24) = -1.5708
    c: PointOnObject(g27,g19)
    c: PointOnObject(g27,g14)
    c: Tangent(g19,g26) = 1.5708
    c: Tangent(g14,g26) = 1.5708
    c: PointOnObject(g29,g14)
    c: PointOnObject(g29,g13)
    c: Tangent(g14,g28) = 1.5708
    c: Tangent(g13,g28) = 1.5708
    c: Horizontal(g30)
    c: PointOnObject(g32,g13)
    c: PointOnObject(g32,g30)
    c: Tangent(g13,g31) = 1.5708
    c: Tangent(g30,g31) = 1.5708
    c: PointOnObject(g34,g30)
    c: PointOnObject(g34,g12)
    c: Tangent(g30,g33) = -1.5708
    c: Tangent(g12,g33) = -1.5708
    c: PointOnObject(g36,g11)
    c: PointOnObject(g36,g12)
    c: Tangent(g11,g35) = 1.5708
    c: Tangent(g12,g35) = 1.5708
    c: Tangent(g10,g37) = -1.5708
    c: Tangent(g21,g37) = 1.5708
    c: PointOnObject(g39,g10)
    c: PointOnObject(g39,g9)
    c: Tangent(g10,g38) = 1.5708
    c: Tangent(g9,g38) = 1.5708
    c: PointOnObject(g41,g15)
    c: PointOnObject(g41,g9)
    c: Tangent(g15,g40) = -1.5708
    c: Tangent(g9,g40) = 1.5708
    c: Tangent(g16,g42) = 1.5708
    c: Tangent(g15,g42) = 1.5708
    c: Radius(g22) = 0.5
    c: Equal(g42,g40)
    c: Equal(g40,g22)
    c: Equal(g22,g23)
    c: Equal(g23,g24)
    c: Equal(g24,g26)
    c: Equal(g26,g33)
    c: Equal(g33,g35)
    c: Equal(g35,g37)
    c: Equal(g37,g38)
    c: Equal(g33,g31)
    c: Equal(g28,g26)
    c: Tangent(g43,g44) = -1.5708
    c: Coincident(g43,g60)
    c: Coincident(g44,g45)
    c: Coincident(g45,g46)
    c: Coincident(g46,g47)
    c: Tangent(g47,g48) = 1.5708
    c: Tangent(g48,g49) = 1.5708
    c: Tangent(g49,g50) = 1.5708
    c: Tangent(g50,g51) = 1.5708
    c: Coincident(g51,g52)
    c: Tangent(g52,g53) = 1.5708
    c: Tangent(g53,g54) = 1.5708
    c: Tangent(g54,g55) = 1.5708
    c: Coincident(g55,g56)
    c: Tangent(g56,g57) = 1.5708
    c: Tangent(g57,g58) = 1.5708
    c: Tangent(g58,g59) = 1.5708
    c: Tangent(g59,g60) = -1.5708
    c: Block(g55)
    c: Block(g54)
    c: Block(g53)
    c: Block(g52)
    c: Block(g51)
    c: Block(g50)
    c: Block(g49)
    c: Block(g48)
    c: Block(g47)
    c: Block(g46)
    c: Block(g45)
    c: Block(g44)
    c: Block(g43)
    c: Block(g60)
    c: Block(g59)
    c: Block(g58)
    c: Block(g57)
    c: Block(g21)
    c: Block(g37)
    c: Block(g10)
    c: Block(g38)
    c: Block(g9)
    c: Block(g40)
    c: Block(g15)
    c: Block(g42)
    c: Block(g16)
    c: Block(g18)
    c: Block(g22)
    c: Block(g17)
    c: Block(g23)
    c: Block(g20)
    c: Block(g24)
    c: Block(g26)
    c: Block(g19)
    c: Block(g14)
    c: Block(g28)
    c: Block(g13)
    c: Block(g31)
    c: Block(g30)
    c: Block(g33)
    c: Block(g12)
    c: Block(g35)
